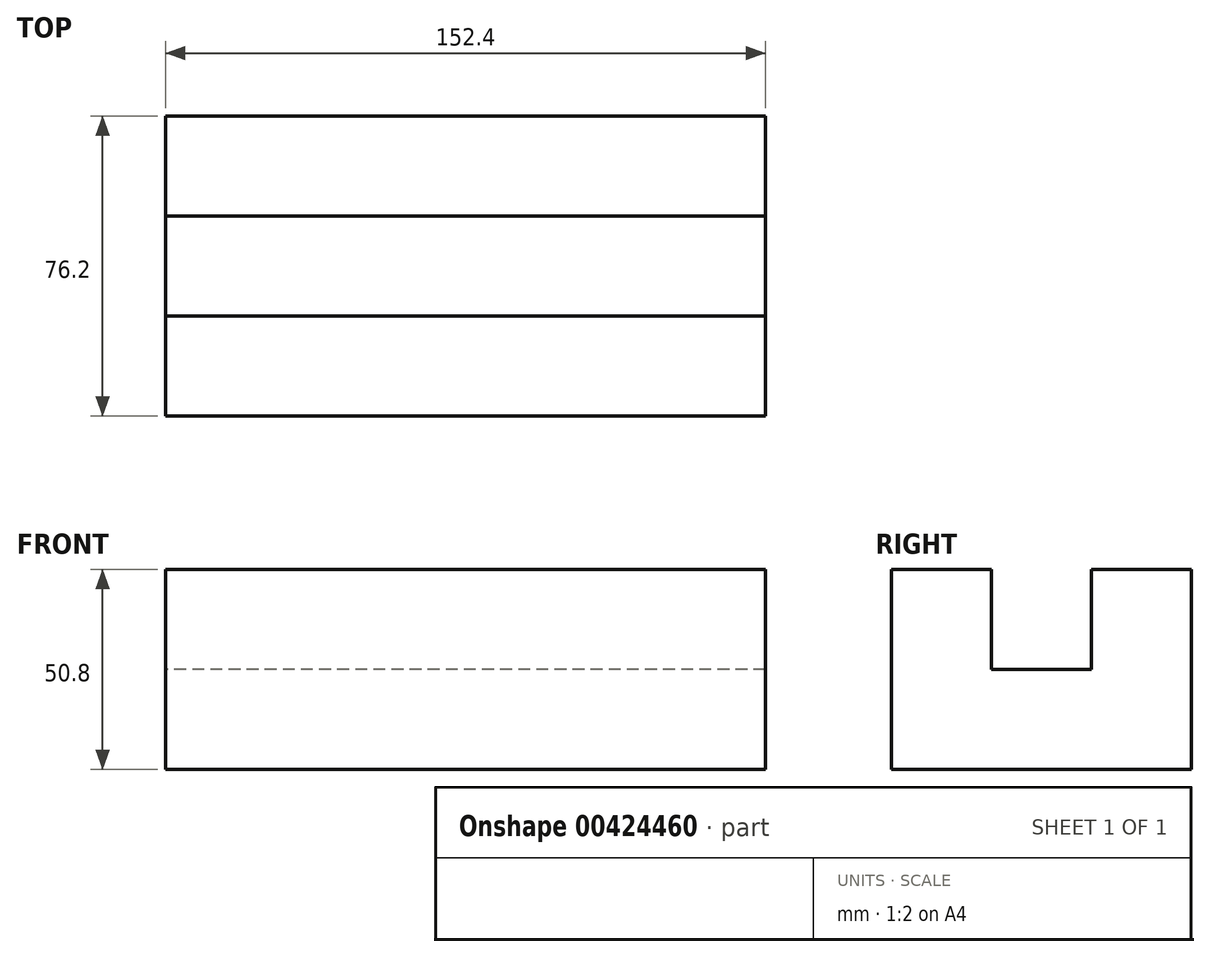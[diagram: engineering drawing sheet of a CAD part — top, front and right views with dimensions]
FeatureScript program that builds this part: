
annotation { "Feature Type Name" : "Feature", "Feature Type Description" : "" }
export const myFeature = defineFeature(function(context is Context, id is Id, definition is map)
    precondition{}
    {
        {
            var Q0;
            Q0=qCreatedBy(makeId("Right.planeOp"),FACE);
            var sketch = newSketch(context, id + "F0", { "sketchPlane" : qUnion([Q0])});
            skLineSegment(sketch, "E0", {"start": v(0, 0) * mm, "end": v(76.2, 0) * mm});
            skLineSegment(sketch, "E1", {"start": v(76.2, 0) * mm, "end": v(76.2, 50.8) * mm});
            skLineSegment(sketch, "E2", {"start": v(76.2, 50.8) * mm, "end": v(50.8, 50.8) * mm});
            skLineSegment(sketch, "E3", {"start": v(50.8, 50.8) * mm, "end": v(50.8, 25.4) * mm});
            skLineSegment(sketch, "E4", {"start": v(50.8, 25.4) * mm, "end": v(25.4, 25.4) * mm});
            skLineSegment(sketch, "E5", {"start": v(25.4, 25.4) * mm, "end": v(25.4, 50.8) * mm});
            skLineSegment(sketch, "E6", {"start": v(25.4, 50.8) * mm, "end": v(0, 50.8) * mm});
            skLineSegment(sketch, "E7", {"start": v(0, 50.8) * mm, "end": v(0, 0) * mm});
            skSolve(sketch);
        }
        {
            var Q0;
            Q0=makeQuery(id+"F0.imprint","IMPRINT",FACE,{"disambiguationData":[TD([[makeQuery(id+"F0.imprint","IMPRINT",EDGE,{"derivedFrom":sQuery(id+"F0.wireOp",EDGE,"E0")}),1.0]])]});
            extrude(context, id + "F1", {"entities" : qUnion([Q0]), "depth" : 152.4 * mm});
        }
    });
